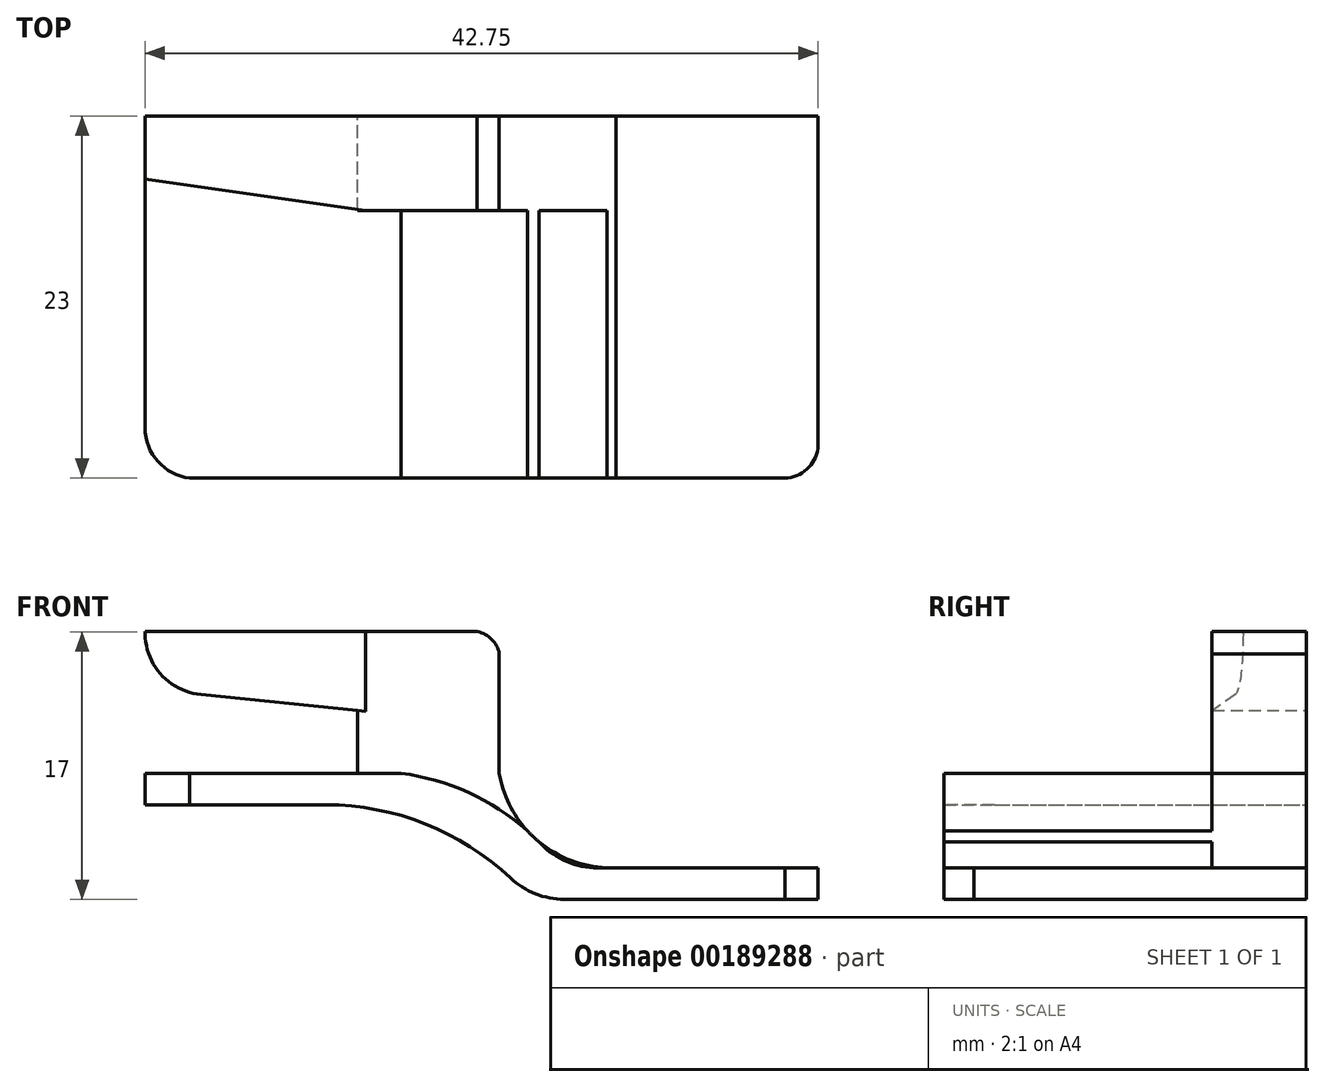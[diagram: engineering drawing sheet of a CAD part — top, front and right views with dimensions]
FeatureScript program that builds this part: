
annotation { "Feature Type Name" : "Feature", "Feature Type Description" : "" }
export const myFeature = defineFeature(function(context is Context, id is Id, definition is map)
    precondition{}
    {
        {
            var Q0;
            Q0=qCreatedBy(makeId("Front.planeOp"),FACE);
            var sketch = newSketch(context, id + "F0", { "sketchPlane" : qUnion([Q0])});
            skLineSegment(sketch, "E0", {"start": v(-1.4, 24.16) * mm, "end": v(-22.5, 24.16) * mm});
            skLineSegment(sketch, "E1", {"start": v(-9, 19.16) * mm, "end": v(-9, 15.16) * mm});
            skLineSegment(sketch, "E2", {"start": v(-9, 15.16) * mm, "end": v(-22.5, 15.16) * mm});
            skLineSegment(sketch, "E3", {"start": v(-22.5, 15.16) * mm, "end": v(-22.5, 13.16) * mm});
            skLineSegment(sketch, "E4", {"start": v(-22.5, 13.16) * mm, "end": v(-11, 13.16) * mm});
            skLineSegment(sketch, "E5", {"start": v(2, 7.16) * mm, "end": v(20.25, 7.16) * mm});
            skLineSegment(sketch, "E6", {"start": v(20.25, 7.16) * mm, "end": v(20.25, 9.16) * mm});
            skLineSegment(sketch, "E7", {"start": v(20.25, 9.16) * mm, "end": v(6.84, 9.16) * mm});
            skLineSegment(sketch, "E8", {"start": v(0, 15.16) * mm, "end": v(0, 22.76) * mm});
            skArc(sketch, "E9", {"start": v(0, 22.76) * mm, "mid": v(-0.48, 23.68) * mm, "end": v(-1.4, 24.16) * mm});
            skArc(sketch, "E10", {"start": v(0, 15.16) * mm, "mid": v(2.58, 10.77) * mm, "end": v(7.42, 9.16) * mm});
            skPoint(sketch, "E11.orphan", {"position": v(0, 24.16) * mm});
            skLineSegment(sketch, "E12", {"start": v(-9, 19.16) * mm, "end": v(0, 19.16) * mm, "construction": true});
            skLineSegment(sketch, "E13", {"start": v(-9, 19.16) * mm, "end": v(-18.95, 20.16) * mm});
            skArc(sketch, "E14", {"start": v(-22.5, 24.16) * mm, "mid": v(-21.5, 21.47) * mm, "end": v(-18.95, 20.16) * mm});
            skArc(sketch, "E15", {"start": v(2, 7.16) * mm, "mid": v(-3.84, 11.6) * mm, "end": v(-11, 13.16) * mm});
            skLineSegment(sketch, "E16", {"start": v(-9, 15.16) * mm, "end": v(0, 15.16) * mm, "construction": true});
            skLineSegment(sketch, "E17", {"start": v(6.84, 9.16) * mm, "end": v(0, 9.16) * mm, "construction": true});
            skArc(sketch, "E18", {"start": v(3.93, 9.16) * mm, "mid": v(-0.54, 13.2) * mm, "end": v(-6.23, 15.16) * mm});
            skLineSegment(sketch, "E19", {"start": v(-6.23, 15.16) * mm, "end": v(-9, 15.16) * mm});
            skLineSegment(sketch, "E20", {"start": v(3.93, 9.16) * mm, "end": v(6.84, 9.16) * mm});
            skSolve(sketch);
        }
        {
            var Q0;
            Q0=makeQuery(id+"F0.imprint","IMPRINT",FACE,{"disambiguationData":[TD([[makeQuery(id+"F0.imprint","IMPRINT",EDGE,{"derivedFrom":sQuery(id+"F0.wireOp",EDGE,"E0")}),1.0]])]});
            extrude(context, id + "F1", {"entities" : qUnion([Q0]), "depth" : 6 * mm, "offsetDistance" : 25 * mm});
        }
        {
            var Q0;
            Q0=makeQuery(id+"F0.imprint","IMPRINT",FACE,{"disambiguationData":[TD([[makeQuery(id+"F0.imprint","IMPRINT",EDGE,{"derivedFrom":sQuery(id+"F0.wireOp",EDGE,"E2")}),1.0]])]});
            extrude(context, id + "F2", {"entities" : qUnion([Q0]), "operationType" : NewBodyOperationType.ADD, "depth" : 23 * mm, "offsetDistance" : 25 * mm});
        }
        {
            var Q0;
            {var subQ0=sQuery(id+"F0.wireOp",EDGE,"E20");Q0=makeQuery(id+"F0.imprint","IMPRINT",FACE,{"disambiguationData":[TD([[makeQuery(id+"F0.imprint","IMPRINT",EDGE,{"derivedFrom":subQ0}),1.0]])]});}
            extrude(context, id + "F3", {"entities" : qUnion([Q0]), "operationType" : NewBodyOperationType.ADD, "depth" : 6 * mm, "offsetDistance" : 25 * mm});
        }
        {
            var Q0;
            Q0=makeQuery(id+"F2.opExtrude","SWEPT_EDGE",EDGE,{"disambiguationData":[OSD([sQuery(id+"F0.wireOp",EDGE,"E18"),sQuery(id+"F0.wireOp",EDGE,"E20")])]});
            fillet(context, id + "F4", {"entities" : qUnion([Q0]), "radius" : 5 * mm, "tangentPropagation" : true, "allowEdgeOverflow" : false});
        }
        {
            var Q0;
            Q0=makeQuery(id+"F1.opExtrude","SWEPT_FACE",FACE,{"disambiguationData":[OSD([sQuery(id+"F0.wireOp",EDGE,"E0")])]});
            var sketch = newSketch(context, id + "F5", { "sketchPlane" : qUnion([Q0])});
            skPoint(sketch, "E21", {"position": v(-22.5, -4) * mm});
            skPoint(sketch, "E22", {"position": v(-8.5, -6) * mm});
            skLineSegment(sketch, "E23", {"start": v(-22.5, -4) * mm, "end": v(-8.5, -6) * mm});
            skLineSegment(sketch, "E24", {"start": v(-22.5, -6) * mm, "end": v(-22.5, -4) * mm});
            skLineSegment(sketch, "E25", {"start": v(-22.5, -6) * mm, "end": v(-8.5, -6) * mm});
            skLineSegment(sketch, "E26.bottom", {"start": v(-22.5, -4) * mm, "end": v(-23.31, -4) * mm});
            skLineSegment(sketch, "E26.top", {"start": v(-22.5, -6) * mm, "end": v(-23.31, -6) * mm});
            skLineSegment(sketch, "E26.left", {"start": v(-22.5, -4) * mm, "end": v(-22.5, -6) * mm});
            skLineSegment(sketch, "E26.right", {"start": v(-23.31, -4) * mm, "end": v(-23.31, -6) * mm});
            skSolve(sketch);
        }
        {
            var Q0;
            Q0=makeQuery(id+"F5.imprint","IMPRINT",FACE,{"disambiguationData":[TD([[makeQuery(id+"F5.imprint","IMPRINT",EDGE,{"derivedFrom":sQuery(id+"F5.wireOp",EDGE,"E23")}),-1.0]])]});
            var Q1;
            Q1=makeQuery(id+"F5.imprint","IMPRINT",FACE,{"disambiguationData":[TD([[makeQuery(id+"F5.imprint","IMPRINT",EDGE,{"derivedFrom":sQuery(id+"F5.wireOp",EDGE,"E26.bottom")}),1.0]])]});
            var Q2;
            Q2=makeQuery(id+"F1.opExtrude","SWEPT_FACE",FACE,{"disambiguationData":[OSD([sQuery(id+"F0.wireOp",EDGE,"E13")])]});
            extrude(context, id + "F6", {"entities" : qUnion([Q0, Q1]), "operationType" : NewBodyOperationType.REMOVE, "endBound" : BoundingType.UP_TO_SURFACE, "oppositeDirection" : true, "depth" : 25 * mm, "endBoundEntityFace" : qUnion([Q2]), "offsetDistance" : 25 * mm});
        }
        {
            var Q0;
            Q0=makeQuery(id+"F2.opExtrude","SWEPT_FACE",FACE,{"disambiguationData":[OSD([sQuery(id+"F0.wireOp",EDGE,"E2"),sQuery(id+"F0.wireOp",EDGE,"E19")])]});
            var sketch = newSketch(context, id + "F7", { "sketchPlane" : qUnion([Q0])});
            skPoint(sketch, "E27", {"position": v(-22.5, -19.8) * mm});
            skPoint(sketch, "E28", {"position": v(-19.66, -23) * mm});
            skArc(sketch, "E29", {"start": v(-22.5, -19.8) * mm, "mid": v(-21.68, -21.94) * mm, "end": v(-19.66, -23) * mm});
            skLineSegment(sketch, "E30", {"start": v(-22.5, -19.8) * mm, "end": v(-22.5, -23) * mm});
            skLineSegment(sketch, "E31", {"start": v(-22.5, -23) * mm, "end": v(-19.66, -23) * mm});
            skSolve(sketch);
        }
        {
            var Q0;
            Q0=makeQuery(id+"F7.imprint","IMPRINT",FACE,{"disambiguationData":[TD([[makeQuery(id+"F7.imprint","IMPRINT",EDGE,{"derivedFrom":sQuery(id+"F7.wireOp",EDGE,"E29")}),-1.0]])]});
            var Q1;
            Q1=makeQuery(id+"F2.opExtrude","SWEPT_FACE",FACE,{"disambiguationData":[OSD([sQuery(id+"F0.wireOp",EDGE,"E4")])]});
            extrude(context, id + "F8", {"entities" : qUnion([Q0]), "operationType" : NewBodyOperationType.REMOVE, "endBound" : BoundingType.UP_TO_SURFACE, "oppositeDirection" : true, "depth" : 25 * mm, "endBoundEntityFace" : qUnion([Q1]), "offsetDistance" : 25 * mm});
        }
        {
            var Q0;
            Q0=makeQuery(id+"F2.opExtrude","SWEPT_FACE",FACE,{"disambiguationData":[OSD([sQuery(id+"F0.wireOp",EDGE,"E7")])]});
            var sketch = newSketch(context, id + "F9", { "sketchPlane" : qUnion([Q0])});
            skPoint(sketch, "E32", {"position": v(17.93, -23) * mm});
            skPoint(sketch, "E33", {"position": v(20.25, -21.11) * mm});
            skArc(sketch, "E34", {"start": v(17.93, -23) * mm, "mid": v(19.45, -22.5) * mm, "end": v(20.25, -21.11) * mm});
            skLineSegment(sketch, "E35", {"start": v(17.93, -23) * mm, "end": v(20.25, -23) * mm});
            skLineSegment(sketch, "E36", {"start": v(20.25, -23) * mm, "end": v(20.25, -21.11) * mm});
            skSolve(sketch);
        }
        {
            var Q0;
            {var subQ0=sQuery(id+"F9.wireOp",EDGE,"E36");Q0=makeQuery(id+"F9.imprint","IMPRINT",FACE,{"disambiguationData":[TD([[makeQuery(id+"F9.imprint","IMPRINT",EDGE,{"derivedFrom":subQ0}),1.0]])]});}
            var Q1;
            Q1=makeQuery(id+"F2.opExtrude","SWEPT_FACE",FACE,{"disambiguationData":[OSD([sQuery(id+"F0.wireOp",EDGE,"E5")])]});
            extrude(context, id + "F10", {"entities" : qUnion([Q0]), "operationType" : NewBodyOperationType.REMOVE, "endBound" : BoundingType.UP_TO_SURFACE, "oppositeDirection" : true, "depth" : 25 * mm, "endBoundEntityFace" : qUnion([Q1]), "offsetDistance" : 25 * mm});
        }
        {
            var Q0;
            Q0=makeQuery(id+"F2.opExtrude","SWEPT_EDGE",EDGE,{"disambiguationData":[OSD([sQuery(id+"F0.wireOp",EDGE,"E5"),sQuery(id+"F0.wireOp",EDGE,"E15")])]});
            fillet(context, id + "F11", {"entities" : qUnion([Q0]), "radius" : 5 * mm, "tangentPropagation" : true, "allowEdgeOverflow" : false});
        }
    });
